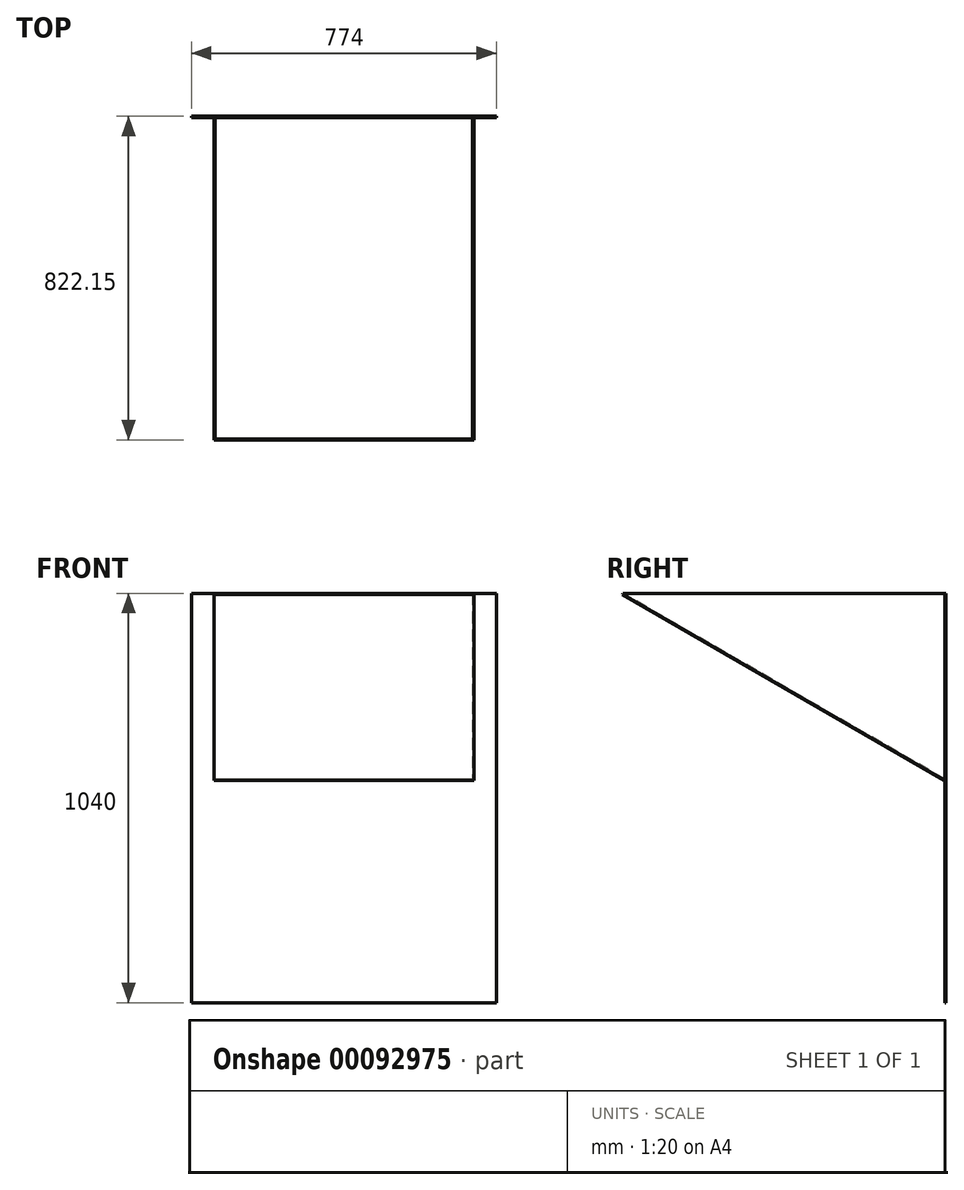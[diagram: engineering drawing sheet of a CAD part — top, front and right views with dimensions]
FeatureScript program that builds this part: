
annotation { "Feature Type Name" : "Feature", "Feature Type Description" : "" }
export const myFeature = defineFeature(function(context is Context, id is Id, definition is map)
    precondition{}
    {
        {
            var Q0;
            Q0=qCreatedBy(makeId("Front.planeOp"),FACE);
            var sketch = newSketch(context, id + "F0", { "sketchPlane" : qUnion([Q0])});
            skLineSegment(sketch, "E0.0", {"start": v(-387, 165.7) * mm, "end": v(-387, 1045) * mm});
            skLineSegment(sketch, "E1.0", {"start": v(-387, 1045) * mm, "end": v(-327, 1045) * mm});
            skLineSegment(sketch, "E2.0", {"start": v(-327, 572.93) * mm, "end": v(-327, 1045) * mm});
            skLineSegment(sketch, "E3.0", {"start": v(327, 1045) * mm, "end": v(327, 572.93) * mm});
            skLineSegment(sketch, "E4.0", {"start": v(327, 1045) * mm, "end": v(387, 1045) * mm});
            skLineSegment(sketch, "E5.0", {"start": v(387, 165.7) * mm, "end": v(387, 1045) * mm});
            skLineSegment(sketch, "E6", {"start": v(-327, 572.93) * mm, "end": v(327, 572.93) * mm});
            skLineSegment(sketch, "E7", {"start": v(-387, 165.7) * mm, "end": v(-387, 5) * mm});
            skLineSegment(sketch, "E8", {"start": v(387, 165.7) * mm, "end": v(387, 5) * mm});
            skLineSegment(sketch, "E9", {"start": v(-387, 1045) * mm, "end": v(387, 1045) * mm, "construction": true});
            skLineSegment(sketch, "E10", {"start": v(-387, 5) * mm, "end": v(387, 5) * mm});
            skSolve(sketch);
        }
        {
            var Q0;
            Q0 = qSketchRegion(id + "F0", true);
            extrude(context, id + "F1", {"entities" : qUnion([Q0]), "depth" : 3 * mm});
        }
        {
            var Q0;
            Q0=makeQuery(id+"F1.opExtrude","SWEPT_FACE",FACE,{"disambiguationData":[OSD([sQuery(id+"F0.wireOp",EDGE,"E3.0")])]});
            var sketch = newSketch(context, id + "F2", { "sketchPlane" : qUnion([Q0])});
            skLineSegment(sketch, "E11", {"start": v(0, 1045) * mm, "end": v(820.65, 1045) * mm});
            skLineSegment(sketch, "E12.0", {"start": v(3, 572.93) * mm, "end": v(0, 572.93) * mm, "construction": true});
            skLineSegment(sketch, "E13", {"start": v(0, 1045) * mm, "end": v(0, 572.93) * mm});
            skLineSegment(sketch, "E14", {"start": v(3, 572.93) * mm, "end": v(820.65, 1045) * mm});
            skLineSegment(sketch, "E15", {"start": v(3, 572.93) * mm, "end": v(0, 572.93) * mm});
            skSolve(sketch);
        }
        {
            var Q0;
            Q0 = qSketchRegion(id + "F2", true);
            var Q1;
            {var subQ2=sQuery(id+"F2.wireOp",EDGE,"E14");Q1=makeQuery(id+"F2.imprint","IMPRINT",FACE,{"disambiguationData":[TD([[makeQuery(id+"F2.imprint","IMPRINT",EDGE,{"derivedFrom":subQ2}),1.0]])]});}
            extrude(context, id + "F3", {"entities" : qUnion([Q0, Q1]), "operationType" : NewBodyOperationType.ADD, "oppositeDirection" : true, "depth" : 3 * mm});
        }
        {
            var Q0;
            Q0=makeQuery(id+"F1.opExtrude","SWEPT_FACE",FACE,{"disambiguationData":[OSD([sQuery(id+"F0.wireOp",EDGE,"E2.0")])]});
            var sketch = newSketch(context, id + "F4", { "sketchPlane" : qUnion([Q0])});
            skLineSegment(sketch, "E16.0", {"start": v(-3, 1045) * mm, "end": v(-820.65, 1045) * mm});
            skLineSegment(sketch, "E17.0", {"start": v(-3, 572.93) * mm, "end": v(-820.65, 1045) * mm});
            skLineSegment(sketch, "E18.0", {"start": v(-3, 572.93) * mm, "end": v(0, 572.93) * mm});
            skLineSegment(sketch, "E19.0", {"start": v(0, 1045) * mm, "end": v(0, 572.93) * mm});
            skLineSegment(sketch, "E20.0", {"start": v(-3, 1045) * mm, "end": v(0, 1045) * mm});
            skSolve(sketch);
        }
        {
            var Q0;
            Q0 = qSketchRegion(id + "F4", true);
            extrude(context, id + "F5", {"entities" : qUnion([Q0]), "operationType" : NewBodyOperationType.ADD, "oppositeDirection" : true, "depth" : 3 * mm});
        }
        {
            var Q0;
            Q0=makeQuery(id+"F5.opExtrude","SWEPT_FACE",FACE,{"disambiguationData":[OSD([sQuery(id+"F4.wireOp",EDGE,"E17.0")])]});
            var sketch = newSketch(context, id + "F6", { "sketchPlane" : qUnion([Q0])});
            skLineSegment(sketch, "E21.0", {"start": v(-330, 288.69) * mm, "end": v(-330, 1233.2) * mm});
            skLineSegment(sketch, "E22.0", {"start": v(330, 288.69) * mm, "end": v(330, 1233.2) * mm});
            skLineSegment(sketch, "E23", {"start": v(-330, 1233.2) * mm, "end": v(330, 1233.2) * mm});
            skLineSegment(sketch, "E24", {"start": v(-330, 288.69) * mm, "end": v(330, 288.69) * mm});
            skSolve(sketch);
        }
        {
            var Q0;
            Q0 = qSketchRegion(id + "F6", true);
            extrude(context, id + "F7", {"entities" : qUnion([Q0]), "operationType" : NewBodyOperationType.ADD, "depth" : 3 * mm});
        }
        {
            var Q0;
            Q0 = qSketchRegion(id + "F6", true);
            extrude(context, id + "F8", {"entities" : qUnion([Q0]), "operationType" : NewBodyOperationType.ADD, "depth" : 3 * mm});
        }
    });
